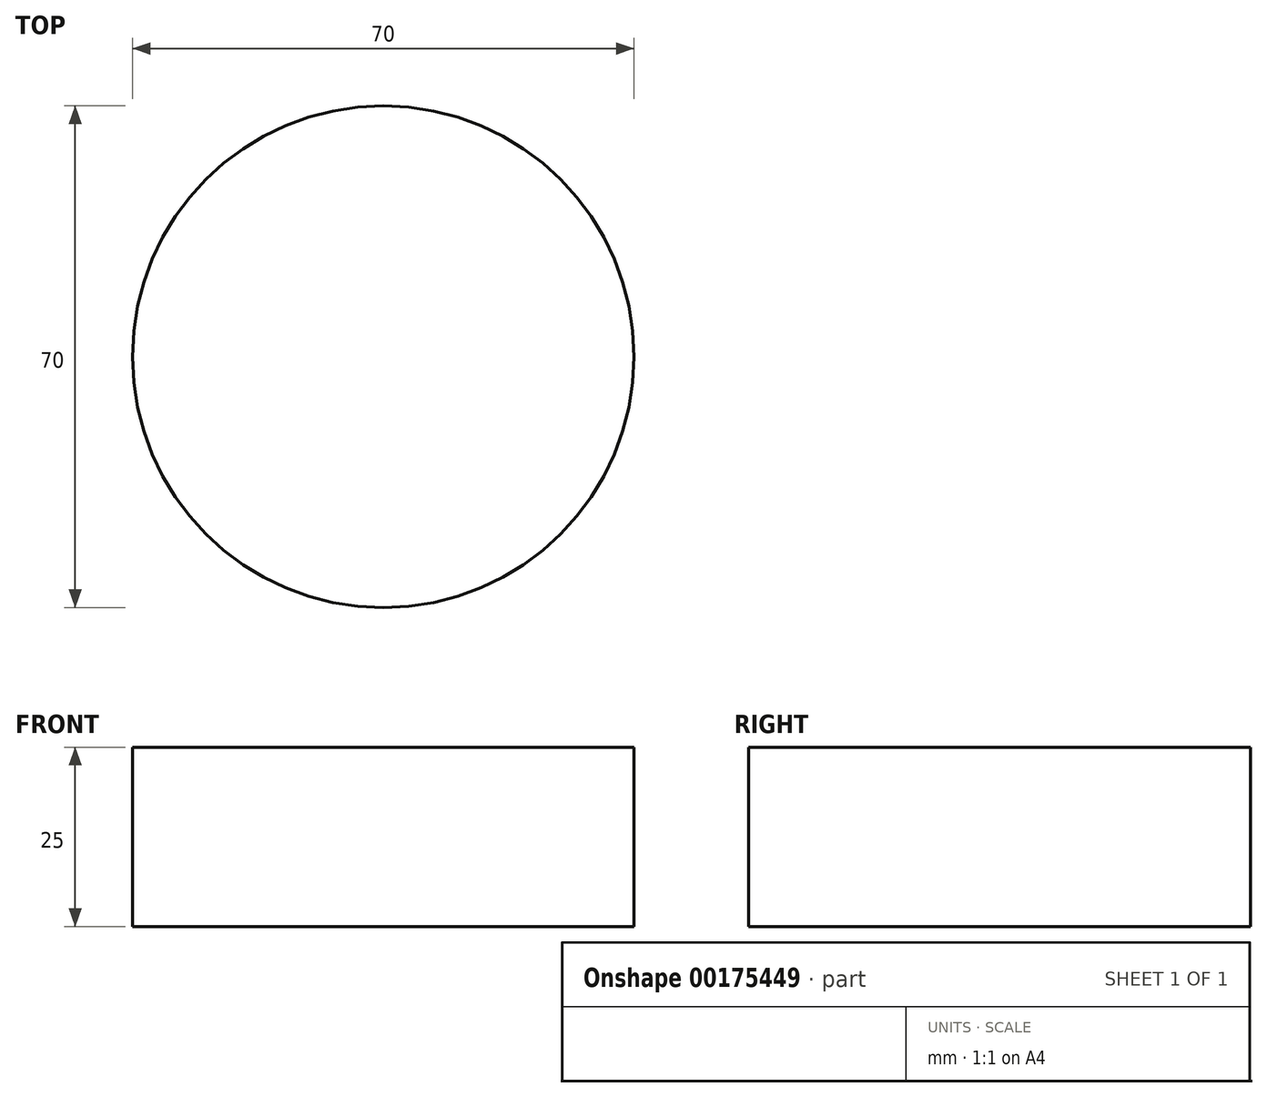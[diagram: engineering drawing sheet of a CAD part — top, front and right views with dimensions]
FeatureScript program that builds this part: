
annotation { "Feature Type Name" : "Feature", "Feature Type Description" : "" }
export const myFeature = defineFeature(function(context is Context, id is Id, definition is map)
    precondition{}
    {
        {
            var Q0;
            Q0=qCreatedBy(makeId("Top.planeOp"),FACE);
            var sketch = newSketch(context, id + "F0", { "sketchPlane" : qUnion([Q0])});
            skCircle(sketch, "E0", {"center": v(-30.36, 27.32) * mm, "radius": 35 * mm});
            skSolve(sketch);
        }
        {
            var Q0;
            Q0=makeQuery(id+"F0.imprint","IMPRINT",FACE,{"disambiguationData":[TD([[makeQuery(id+"F0.imprint","IMPRINT",EDGE,{"derivedFrom":sQuery(id+"F0.wireOp",EDGE,"E0")}),1.0]])]});
            extrude(context, id + "F1", {"entities" : qUnion([Q0]), "depth" : 25 * mm});
        }
    });
